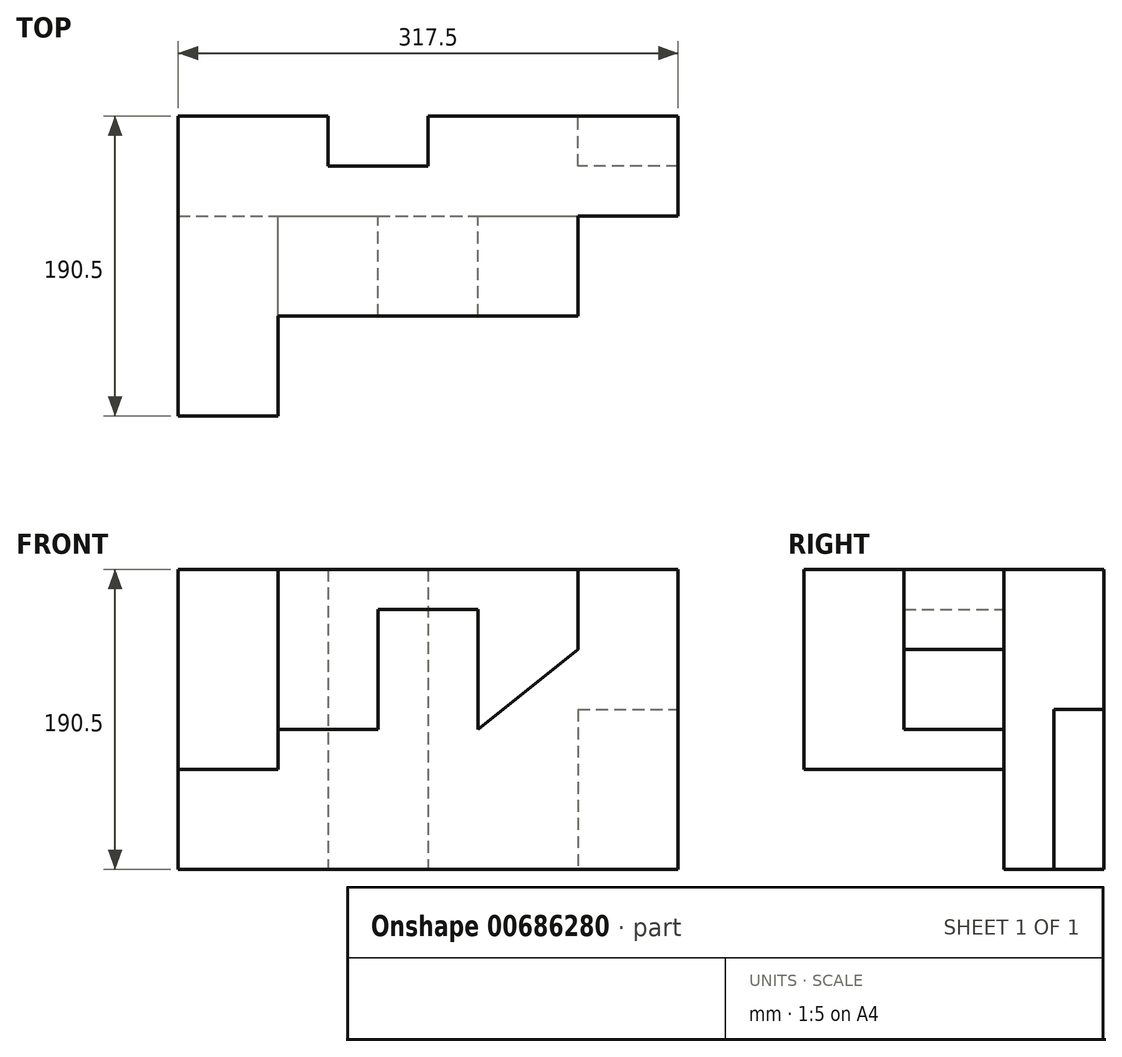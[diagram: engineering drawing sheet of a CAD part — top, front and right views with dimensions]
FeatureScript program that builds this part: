
annotation { "Feature Type Name" : "Feature", "Feature Type Description" : "" }
export const myFeature = defineFeature(function(context is Context, id is Id, definition is map)
    precondition{}
    {
        {
            var Q0;
            Q0=qCreatedBy(makeId("Front.planeOp"),FACE);
            var sketch = newSketch(context, id + "F0", { "sketchPlane" : qUnion([Q0])});
            skLineSegment(sketch, "E0.bottom", {"start": v(-158.75, -95.25) * mm, "end": v(158.75, -95.25) * mm});
            skLineSegment(sketch, "E0.top", {"start": v(-158.75, 95.25) * mm, "end": v(158.75, 95.25) * mm});
            skLineSegment(sketch, "E0.left", {"start": v(-158.75, -95.25) * mm, "end": v(-158.75, 95.25) * mm});
            skLineSegment(sketch, "E0.right", {"start": v(158.75, -95.25) * mm, "end": v(158.75, 95.25) * mm});
            skPoint(sketch, "E0.middle", {"position": v(0, 0) * mm});
            skLineSegment(sketch, "E1", {"start": v(-158.75, -31.75) * mm, "end": v(-95.25, -31.75) * mm});
            skLineSegment(sketch, "E2", {"start": v(-95.25, -31.75) * mm, "end": v(-95.25, 95.25) * mm});
            skLineSegment(sketch, "E3", {"start": v(-95.25, -6.35) * mm, "end": v(-31.75, -6.35) * mm});
            skLineSegment(sketch, "E4", {"start": v(-31.75, -6.35) * mm, "end": v(-31.75, 69.85) * mm});
            skLineSegment(sketch, "E5", {"start": v(-31.75, 69.85) * mm, "end": v(31.75, 69.85) * mm});
            skLineSegment(sketch, "E6", {"start": v(31.75, 69.85) * mm, "end": v(31.75, -6.35) * mm});
            skLineSegment(sketch, "E7", {"start": v(31.75, -6.35) * mm, "end": v(95.25, 44.45) * mm});
            skLineSegment(sketch, "E8", {"start": v(95.25, 44.45) * mm, "end": v(95.25, 95.25) * mm});
            skSolve(sketch);
        }
        {
            var Q0;
            {var subQ3=sQuery(id+"F0.wireOp",EDGE,"E0.bottom");Q0=makeQuery(id+"F0.imprint","IMPRINT",FACE,{"disambiguationData":[TD([[makeQuery(id+"F0.imprint","IMPRINT",EDGE,{"derivedFrom":subQ3}),1.0]])]});}
            var Q1;
            {var subQ0=sQuery(id+"F0.wireOp",EDGE,"E3");Q1=makeQuery(id+"F0.imprint","IMPRINT",FACE,{"disambiguationData":[TD([[makeQuery(id+"F0.imprint","IMPRINT",EDGE,{"derivedFrom":subQ0}),1.0]])]});}
            var Q2;
            {var subQ1=sQuery(id+"F0.wireOp",EDGE,"E1");Q2=makeQuery(id+"F0.imprint","IMPRINT",FACE,{"disambiguationData":[TD([[makeQuery(id+"F0.imprint","IMPRINT",EDGE,{"derivedFrom":subQ1}),1.0]])]});}
            extrude(context, id + "F1", {"entities" : qUnion([Q0, Q1, Q2]), "oppositeDirection" : true, "depth" : 63.5 * mm, "offsetDistance" : 25.4 * mm});
        }
        {
            var Q0;
            {var subQ1=sQuery(id+"F0.wireOp",EDGE,"E1");Q0=makeQuery(id+"F0.imprint","IMPRINT",FACE,{"disambiguationData":[TD([[makeQuery(id+"F0.imprint","IMPRINT",EDGE,{"derivedFrom":subQ1}),1.0]])]});}
            extrude(context, id + "F2", {"entities" : qUnion([Q0]), "operationType" : NewBodyOperationType.ADD, "depth" : 127 * mm, "offsetDistance" : 25.4 * mm});
        }
        {
            var Q0;
            {var subQ0=sQuery(id+"F0.wireOp",EDGE,"E3");Q0=makeQuery(id+"F0.imprint","IMPRINT",FACE,{"disambiguationData":[TD([[makeQuery(id+"F0.imprint","IMPRINT",EDGE,{"derivedFrom":subQ0}),1.0]])]});}
            extrude(context, id + "F3", {"entities" : qUnion([Q0]), "operationType" : NewBodyOperationType.ADD, "depth" : 63.5 * mm, "offsetDistance" : 25.4 * mm});
        }
        {
            var Q0;
            Q0=makeQuery(id+"F1.opExtrude","SWEPT_FACE",FACE,{"disambiguationData":[OSD([sQuery(id+"F0.wireOp",EDGE,"E0.bottom")])]});
            var sketch = newSketch(context, id + "F4", { "sketchPlane" : qUnion([Q0])});
            skLineSegment(sketch, "E9.bottom", {"start": v(0, -63.5) * mm, "end": v(-63.5, -63.5) * mm});
            skLineSegment(sketch, "E9.top", {"start": v(0, -31.75) * mm, "end": v(-63.5, -31.75) * mm});
            skLineSegment(sketch, "E9.left", {"start": v(0, -63.5) * mm, "end": v(0, -31.75) * mm});
            skLineSegment(sketch, "E9.right", {"start": v(-63.5, -63.5) * mm, "end": v(-63.5, -31.75) * mm});
            skLineSegment(sketch, "E10", {"start": v(158.75, -31.75) * mm, "end": v(95.25, -31.75) * mm});
            skLineSegment(sketch, "E11", {"start": v(95.25, -31.75) * mm, "end": v(95.25, -63.5) * mm});
            skSolve(sketch);
        }
        {
            var Q0;
            {var subQ0=sQuery(id+"F4.wireOp",EDGE,"E10");Q0=makeQuery(id+"F4.imprint","IMPRINT",FACE,{"disambiguationData":[TD([[makeQuery(id+"F4.imprint","IMPRINT",EDGE,{"derivedFrom":subQ0}),1.0]])]});}
            extrude(context, id + "F5", {"entities" : qUnion([Q0]), "operationType" : NewBodyOperationType.REMOVE, "oppositeDirection" : true, "depth" : 101.6 * mm, "offsetDistance" : 25.4 * mm});
        }
        {
            var Q0;
            Q0=makeQuery(id+"F4.imprint","IMPRINT",FACE,{"disambiguationData":[TD([[makeQuery(id+"F4.imprint","IMPRINT",EDGE,{"derivedFrom":sQuery(id+"F4.wireOp",EDGE,"E9.bottom")}),1.0]])]});
            extrude(context, id + "F6", {"entities" : qUnion([Q0]), "operationType" : NewBodyOperationType.REMOVE, "endBound" : BoundingType.THROUGH_ALL, "oppositeDirection" : true, "depth" : 243.33 * mm, "offsetDistance" : 25.4 * mm});
        }
    });
